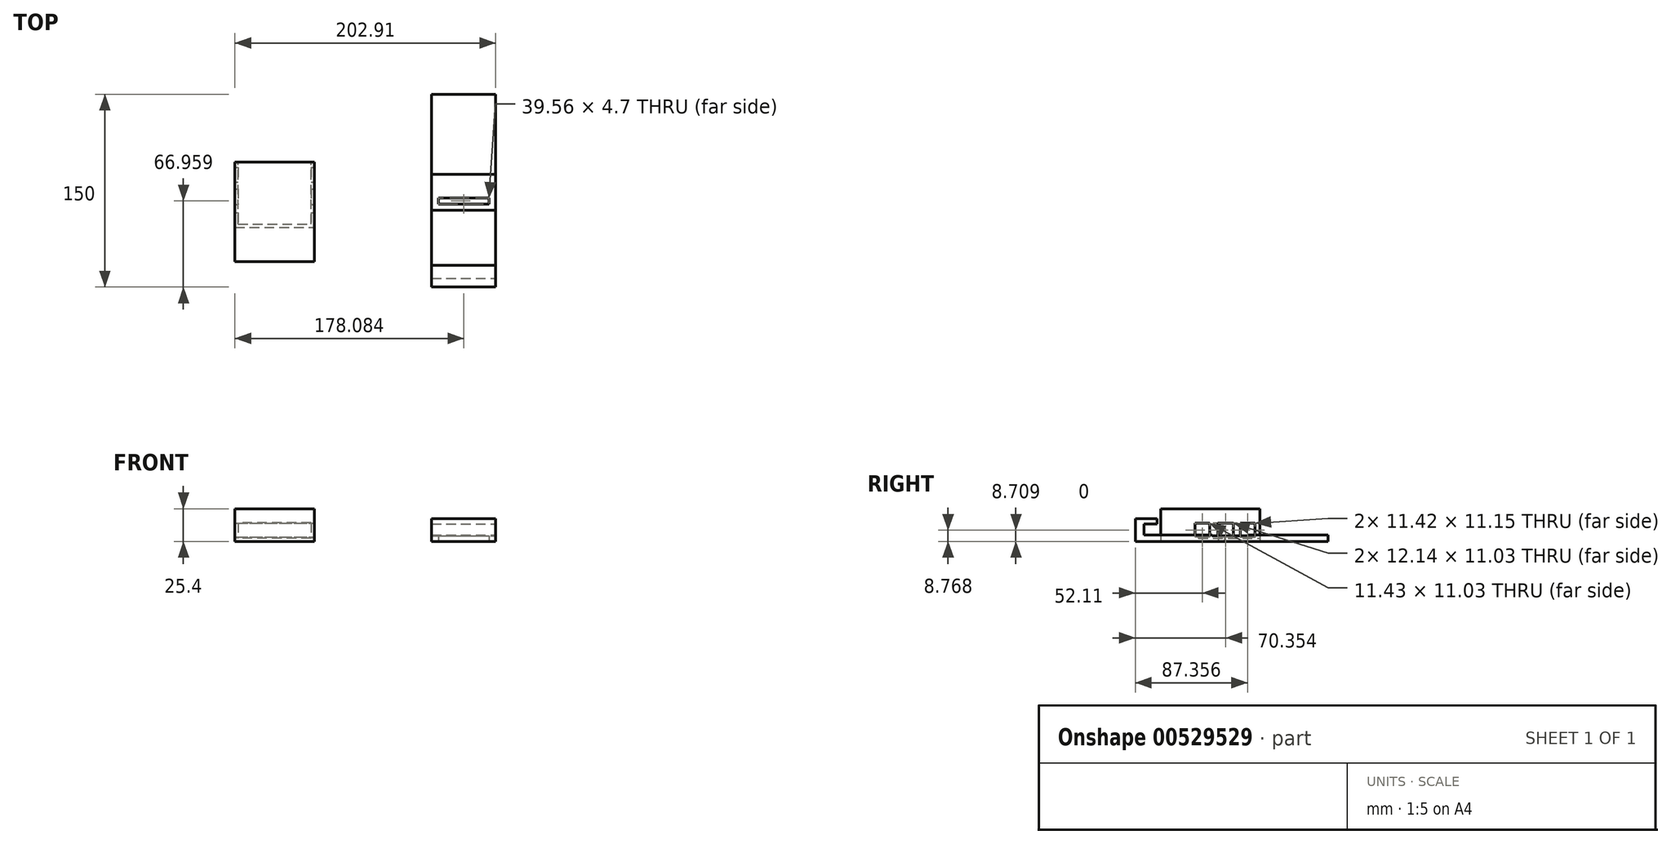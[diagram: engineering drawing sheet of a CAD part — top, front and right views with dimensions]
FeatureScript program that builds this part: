
annotation { "Feature Type Name" : "Feature", "Feature Type Description" : "" }
export const myFeature = defineFeature(function(context is Context, id is Id, definition is map)
    precondition{}
    {
        {
            var Q0;
            Q0=qCreatedBy(makeId("Top.planeOp"),FACE);
            var sketch = newSketch(context, id + "F0", { "sketchPlane" : qUnion([Q0])});
            skLineSegment(sketch, "E0.bottom", {"start": v(59.03, 64.61) * mm, "end": v(109.03, 64.61) * mm});
            skLineSegment(sketch, "E0.top", {"start": v(59.03, -85.39) * mm, "end": v(109.03, -85.39) * mm});
            skLineSegment(sketch, "E0.left", {"start": v(59.03, 64.61) * mm, "end": v(59.03, -85.39) * mm});
            skLineSegment(sketch, "E0.right", {"start": v(109.03, 64.61) * mm, "end": v(109.03, -85.39) * mm});
            skSolve(sketch);
        }
        {
            var Q0;
            Q0=makeQuery(id+"F0.imprint","IMPRINT",FACE,{"disambiguationData":[TD([[makeQuery(id+"F0.imprint","IMPRINT",EDGE,{"derivedFrom":sQuery(id+"F0.wireOp",EDGE,"E0.bottom")}),-1.0]])]});
            extrude(context, id + "F1", {"entities" : qUnion([Q0]), "depth" : 5 * mm, "offsetDistance" : 25.4 * mm});
        }
        {
            var Q0;
            Q0=makeQuery(id+"F1.opExtrude","SWEPT_FACE",FACE,{"disambiguationData":[OSD([sQuery(id+"F0.wireOp",EDGE,"E0.right")])]});
            var sketch = newSketch(context, id + "F2", { "sketchPlane" : qUnion([Q0])});
            skLineSegment(sketch, "E1.bottom", {"start": v(-8.72, 4.32) * mm, "end": v(-25.7, 4.32) * mm});
            skLineSegment(sketch, "E1.top", {"start": v(-8.72, 10.08) * mm, "end": v(-25.7, 10.08) * mm});
            skLineSegment(sketch, "E1.left", {"start": v(-8.72, 4.32) * mm, "end": v(-8.72, 10.08) * mm});
            skLineSegment(sketch, "E1.right", {"start": v(-25.7, 4.32) * mm, "end": v(-25.7, 10.08) * mm});
            skSolve(sketch);
        }
        {
            var Q0;
            Q0 = qSketchRegion(id + "F2", true);
            extrude(context, id + "F3", {"entities" : qUnion([Q0]), "operationType" : NewBodyOperationType.REMOVE, "oppositeDirection" : true, "depth" : 56.64 * mm, "offsetDistance" : 25.4 * mm});
        }
        {
            var Q0;
            Q0=makeQuery(id+"F1.opExtrude","SWEPT_FACE",FACE,{"disambiguationData":[OSD([sQuery(id+"F0.wireOp",EDGE,"E0.left")])]});
            var sketch = newSketch(context, id + "F4", { "sketchPlane" : qUnion([Q0])});
            skLineSegment(sketch, "E2.bottom", {"start": v(25.7, 4.32) * mm, "end": v(-2.35, 4.32) * mm});
            skLineSegment(sketch, "E2.top", {"start": v(25.7, 5) * mm, "end": v(-2.35, 5) * mm});
            skLineSegment(sketch, "E2.left", {"start": v(25.7, 4.32) * mm, "end": v(25.7, 5) * mm});
            skLineSegment(sketch, "E2.right", {"start": v(-2.35, 4.32) * mm, "end": v(-2.35, 5) * mm});
            skSolve(sketch);
        }
        {
            var Q0;
            Q0=makeQuery(id+"F4.imprint","IMPRINT",FACE,{"disambiguationData":[TD([[makeQuery(id+"F4.imprint","IMPRINT",EDGE,{"derivedFrom":sQuery(id+"F4.wireOp",EDGE,"E2.top")}),-1.0]])]});
            extrude(context, id + "F5", {"entities" : qUnion([Q0]), "operationType" : NewBodyOperationType.REMOVE, "oppositeDirection" : true, "depth" : 60.96 * mm, "offsetDistance" : 25.4 * mm});
        }
        {
            var Q0;
            Q0=makeQuery(id+"F1.opExtrude","CAP_FACE",FACE,{"disambiguationData":[OSD([sQuery(id+"F0.wireOp",EDGE,"E0.bottom"),sQuery(id+"F0.wireOp",EDGE,"E0.top"),sQuery(id+"F0.wireOp",EDGE,"E0.left"),sQuery(id+"F0.wireOp",EDGE,"E0.right")])],"isStart":true});
            var sketch = newSketch(context, id + "F6", { "sketchPlane" : qUnion([Q0])});
            skLineSegment(sketch, "E3.bottom", {"start": v(103.98, 16.08) * mm, "end": v(64.42, 16.08) * mm});
            skLineSegment(sketch, "E3.top", {"start": v(103.98, 20.78) * mm, "end": v(64.42, 20.78) * mm});
            skLineSegment(sketch, "E3.left", {"start": v(103.98, 16.08) * mm, "end": v(103.98, 20.78) * mm});
            skLineSegment(sketch, "E3.right", {"start": v(64.42, 16.08) * mm, "end": v(64.42, 20.78) * mm});
            skSolve(sketch);
        }
        {
            var Q0;
            Q0=makeQuery(id+"F6.imprint","IMPRINT",FACE,{"disambiguationData":[TD([[makeQuery(id+"F6.imprint","IMPRINT",EDGE,{"derivedFrom":sQuery(id+"F6.wireOp",EDGE,"E3.bottom")}),-1.0]])]});
            extrude(context, id + "F7", {"entities" : qUnion([Q0]), "operationType" : NewBodyOperationType.REMOVE, "oppositeDirection" : true, "depth" : 25.4 * mm, "offsetDistance" : 25.4 * mm});
        }
        {
            var Q0;
            {var subQ0=sQuery(id+"F0.wireOp",EDGE,"E0.top");var subQ1=sQuery(id+"F0.wireOp",EDGE,"E0.left");var subQ2=sQuery(id+"F0.wireOp",EDGE,"E0.right");Q0=makeQuery(id+"F3.boolean.opBoolean","SPLIT",FACE,{"disambiguationData":[TD([makeQuery(id+"F1.opExtrude","SWEPT_FACE",FACE,{"disambiguationData":[OSD([subQ0])]})])],"derivedFrom":makeQuery(id+"F1.opExtrude","CAP_FACE",FACE,{"disambiguationData":[OSD([sQuery(id+"F0.wireOp",EDGE,"E0.bottom"),subQ0,subQ1,subQ2])],"isStart":false})});}
            var sketch = newSketch(context, id + "F8", { "sketchPlane" : qUnion([Q0])});
            skLineSegment(sketch, "E4.bottom", {"start": v(59.03, -78.56) * mm, "end": v(109.03, -78.56) * mm});
            skLineSegment(sketch, "E4.top", {"start": v(59.03, -85.39) * mm, "end": v(109.03, -85.39) * mm});
            skLineSegment(sketch, "E4.left", {"start": v(59.03, -78.56) * mm, "end": v(59.03, -85.39) * mm});
            skLineSegment(sketch, "E4.right", {"start": v(109.03, -78.56) * mm, "end": v(109.03, -85.39) * mm});
            skSolve(sketch);
        }
        {
            var Q0;
            Q0=makeQuery(id+"F8.imprint","IMPRINT",FACE,{"disambiguationData":[TD([[makeQuery(id+"F8.imprint","IMPRINT",EDGE,{"derivedFrom":sQuery(id+"F8.wireOp",EDGE,"E4.bottom")}),-1.0]])]});
            extrude(context, id + "F9", {"entities" : qUnion([Q0]), "operationType" : NewBodyOperationType.ADD, "depth" : 12.5 * mm, "offsetDistance" : 25.4 * mm});
        }
        {
            var Q0;
            Q0=makeQuery(id+"F9.opExtrude","SWEPT_FACE",FACE,{"disambiguationData":[OSD([sQuery(id+"F8.wireOp",EDGE,"E4.bottom")])]});
            var sketch = newSketch(context, id + "F10", { "sketchPlane" : qUnion([Q0])});
            skLineSegment(sketch, "E5.bottom", {"start": v(-59.03, 13.65) * mm, "end": v(-109.03, 13.65) * mm});
            skLineSegment(sketch, "E5.top", {"start": v(-59.03, 17.5) * mm, "end": v(-109.03, 17.5) * mm});
            skLineSegment(sketch, "E5.left", {"start": v(-59.03, 13.65) * mm, "end": v(-59.03, 17.5) * mm});
            skLineSegment(sketch, "E5.right", {"start": v(-109.03, 13.65) * mm, "end": v(-109.03, 17.5) * mm});
            skSolve(sketch);
        }
        {
            var Q0;
            Q0=makeQuery(id+"F10.imprint","IMPRINT",FACE,{"disambiguationData":[TD([[makeQuery(id+"F10.imprint","IMPRINT",EDGE,{"derivedFrom":sQuery(id+"F10.wireOp",EDGE,"E5.bottom")}),-1.0]])]});
            extrude(context, id + "F11", {"entities" : qUnion([Q0]), "operationType" : NewBodyOperationType.ADD, "depth" : 10 * mm, "offsetDistance" : 25.4 * mm});
        }
        {
            var Q0;
            Q0=qCreatedBy(makeId("Top.planeOp"),FACE);
            var sketch = newSketch(context, id + "F12", { "sketchPlane" : qUnion([Q0])});
            skLineSegment(sketch, "E6.bottom", {"start": v(-93.88, 11.7) * mm, "end": v(-32.15, 11.7) * mm});
            skLineSegment(sketch, "E6.top", {"start": v(-93.88, -65.48) * mm, "end": v(-32.15, -65.48) * mm});
            skLineSegment(sketch, "E6.left", {"start": v(-93.88, 11.7) * mm, "end": v(-93.88, -65.48) * mm});
            skLineSegment(sketch, "E6.right", {"start": v(-32.15, 11.7) * mm, "end": v(-32.15, -65.48) * mm});
            skSolve(sketch);
        }
        {
            var Q0;
            Q0=makeQuery(id+"F12.imprint","IMPRINT",FACE,{"disambiguationData":[TD([[makeQuery(id+"F12.imprint","IMPRINT",EDGE,{"derivedFrom":sQuery(id+"F12.wireOp",EDGE,"E6.bottom")}),-1.0]])]});
            extrude(context, id + "F13", {"entities" : qUnion([Q0]), "depth" : 25.4 * mm, "offsetDistance" : 25.4 * mm});
        }
        {
            var Q0;
            Q0=makeQuery(id+"F13.opExtrude","SWEPT_FACE",FACE,{"disambiguationData":[OSD([sQuery(id+"F12.wireOp",EDGE,"E6.bottom")])]});
            var sketch = newSketch(context, id + "F14", { "sketchPlane" : qUnion([Q0])});
            skLineSegment(sketch, "E7.bottom", {"start": v(34.6, 14.35) * mm, "end": v(91.41, 14.35) * mm});
            skLineSegment(sketch, "E7.top", {"start": v(34.6, 2.41) * mm, "end": v(91.41, 2.41) * mm});
            skLineSegment(sketch, "E7.left", {"start": v(34.6, 14.35) * mm, "end": v(34.6, 2.41) * mm});
            skLineSegment(sketch, "E7.right", {"start": v(91.41, 14.35) * mm, "end": v(91.41, 2.41) * mm});
            skSolve(sketch);
        }
        {
            var Q0;
            Q0=makeQuery(id+"F14.imprint","IMPRINT",FACE,{"disambiguationData":[TD([[makeQuery(id+"F14.imprint","IMPRINT",EDGE,{"derivedFrom":sQuery(id+"F14.wireOp",EDGE,"E7.bottom")}),-1.0]])]});
            extrude(context, id + "F15", {"entities" : qUnion([Q0]), "operationType" : NewBodyOperationType.REMOVE, "oppositeDirection" : true, "depth" : 48 * mm, "offsetDistance" : 25.4 * mm});
        }
        {
            var Q0;
            Q0=makeQuery(id+"F13.opExtrude","SWEPT_FACE",FACE,{"disambiguationData":[OSD([sQuery(id+"F12.wireOp",EDGE,"E6.right")])]});
            var sketch = newSketch(context, id + "F16", { "sketchPlane" : qUnion([Q0])});
            skLineSegment(sketch, "E8.bottom", {"start": v(7.68, 14.28) * mm, "end": v(-3.74, 14.28) * mm});
            skLineSegment(sketch, "E8.top", {"start": v(7.68, 3.14) * mm, "end": v(-3.74, 3.14) * mm});
            skLineSegment(sketch, "E8.left", {"start": v(7.68, 14.28) * mm, "end": v(7.68, 3.14) * mm});
            skLineSegment(sketch, "E8.right", {"start": v(-3.74, 14.28) * mm, "end": v(-3.74, 3.14) * mm});
            skLineSegment(sketch, "E9.bottom", {"start": v(-8.97, 14.28) * mm, "end": v(-21.1, 14.28) * mm});
            skLineSegment(sketch, "E9.top", {"start": v(-8.97, 3.26) * mm, "end": v(-21.1, 3.26) * mm});
            skLineSegment(sketch, "E9.left", {"start": v(-8.97, 14.28) * mm, "end": v(-8.97, 3.26) * mm});
            skLineSegment(sketch, "E9.right", {"start": v(-21.1, 14.28) * mm, "end": v(-21.1, 3.26) * mm});
            skLineSegment(sketch, "E10.bottom", {"start": v(-27.56, 14.28) * mm, "end": v(-39, 14.28) * mm});
            skLineSegment(sketch, "E10.top", {"start": v(-27.56, 3.26) * mm, "end": v(-39, 3.26) * mm});
            skLineSegment(sketch, "E10.left", {"start": v(-27.56, 14.28) * mm, "end": v(-27.56, 3.26) * mm});
            skLineSegment(sketch, "E10.right", {"start": v(-39, 14.28) * mm, "end": v(-39, 3.26) * mm});
            skSolve(sketch);
        }
        {
            var Q0;
            Q0=makeQuery(id+"F16.imprint","IMPRINT",FACE,{"disambiguationData":[TD([[makeQuery(id+"F16.imprint","IMPRINT",EDGE,{"derivedFrom":sQuery(id+"F16.wireOp",EDGE,"E10.bottom")}),1.0]])]});
            var Q1;
            Q1 = qSketchRegion(id + "F16", true);
            extrude(context, id + "F17", {"entities" : qUnion([Q0, Q1]), "operationType" : NewBodyOperationType.REMOVE, "oppositeDirection" : true, "depth" : 64 * mm, "offsetDistance" : 25.4 * mm});
        }
    });
